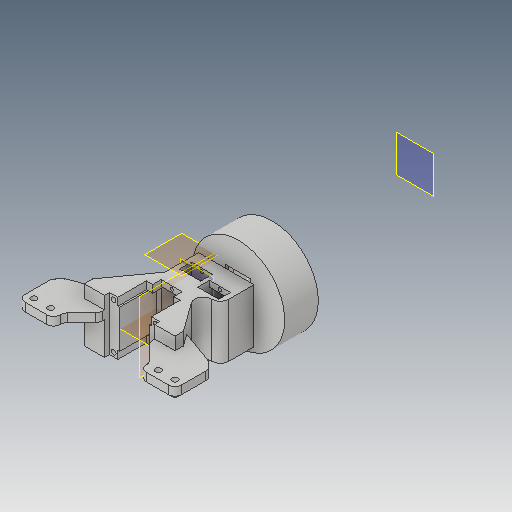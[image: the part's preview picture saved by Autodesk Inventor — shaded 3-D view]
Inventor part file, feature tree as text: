
AUTODESK INVENTOR PART (.ipt)
format: ipt  version: 2018 (Build 220112000, 112)  size: 501,248 bytes
history: native  units: mm
features: extrude x22, sketch x19, plane x6, mirror x5, fillet x2
ambient origin geometry x8: Origin, YZ Plane, XZ Plane, XY Plane, X Axis, Y Axis, Z Axis, Center Point
bodies: Solid1 (feature_tree)
feature tree (54):
  extrude  "base"  Depth=32.0mm
  extrude  "servo_place"  Depth=25.0mm
  extrude  "screws_servo"  Depth=6.25mm
  plane  "Work Plane1"
  extrude  "pilars_top"  Depth=12.5mm
  extrude  "base_top"  Depth=18.0mm
  extrude  "screw_hole"  Depth=2.0mm
  plane  "Work Plane2"
  plane  "Work Plane6"
  plane  "Work Plane5"
  extrude  "Extrusion16"  Depth=17.0mm TaperAngle=0.0deg
  plane  "Work Plane3"
  plane  "Work Plane4"
  mirror  "Mirror1"
  mirror  "Mirror2"
  extrude  "Extrusion18"  Depth=18.0mm
  extrude  "Extrusion19"  Depth=5.0mm TaperAngle=0.0deg
  extrude  "Extrusion20"  Depth=5.0mm TaperAngle=0.0deg
  mirror  "Mirror3"
  mirror  "Mirror4"
  extrude  "Extrusion21"  Depth=5.0mm
  extrude  "Extrusion22"  [1 undecoded]
  extrude  "Extrusion23"  Depth=4.6mm TaperAngle=0.0deg
  extrude  "Extrusion11"  Depth=12.5mm
  extrude  "Extrusion24"  Depth=10.0mm
  fillet  "Fillet5"  Radius=20.0mm
  mirror  "Mirror5"
  extrude  "Extrusion25"  Depth=5.0mm
  extrude  "Extrusion26"  Depth=3.0mm TaperAngle=0.0deg
  extrude  "Extrusion27"  Depth=2.5mm
  fillet  "Fillet6"  Radius=2.8mm
  extrude  "Extrusion28"  Depth=2.0mm
  extrude  "Extrusion29"  Depth=12.5mm
  sketch  "Sketch30"  dims[d117=5.0mm d118=0.0mm d119=11.75mm d120=12.5mm d121=23.5mm d122=12.5mm d123=10.0mm d124=0.0mm d125=7.0mm d126=10.0mm d127=0.0mm d131=27.0mm d132=27.0mm d133=10.0mm d134=0.0mm d135=10.0mm d136=15.0mm d137=3.5mm d138=10.0mm d139=3.5mm d140=3.0mm d141=15.0mm d142=135.0deg d143=6.0mm d144=21.0mm d145=20.0mm d146=6.0mm d147=5.0mm d148=0.0mm d149=4.0mm d150=12.5mm d151=25.0mm d152=5.0mm d153=0.0mm d154=15.0mm d155=0.0mm d156=3.0mm d157=12.5mm d158=12.5mm d159=90.0deg d160=25.0mm d161=90.0deg d162=12.5mm d163=18.0mm d164=0.0mm d165=5.0mm d166=1.8mm d167=90.0deg d168=2.0mm d169=1.8mm d170=90.0deg d171=2.0mm d172=18.0mm d173=0.0mm d174=7.0mm d175=18.0mm d176=0.0mm d177=7.5mm d178=90.0deg d179=50.0mm d180=55.0mm d181=20.0mm d182=0.0mm d183=5.0mm d184=2.0mm d185=90.0deg d186=15.0mm d187=90.0deg d188=2.0mm d189=0.0mm]
  extrude  "Extrusion30"  Depth=23.5mm
  extrude  "Extrusion31"  Depth=12.5mm
  sketch  "Sketch1"  dims[d0=18.0mm d1=32.0mm]
  sketch  "Sketch2"  dims[d2=25.0mm d3=0.0mm d4=11.5mm]
  sketch  "Sketch3"  dims[d5=90.0deg d6=6.25mm]
  sketch  "Sketch6"  dims[d7=23.0mm d8=12.5mm]
  sketch  "Sketch9"  dims[d9=18.0mm d10=0.0mm d11=2.8mm]
  sketch  "Sketch16"  dims[d12=2.0mm d13=2.8mm]
  sketch  "Sketch18"  dims[d14=2.0mm d15=17.0mm d16=0.0mm]
  sketch  "Sketch19"  dims[d26=20.0mm d27=0.0mm d39=18.0mm]
  sketch  "Sketch20"  dims[d40=18.0mm d41=5.0mm d42=0.0mm]
  sketch  "Sketch21"  dims[d47=5.0mm d48=0.0mm d55=5.0mm d56=0.0mm]
  sketch  "Sketch22"  dims[d60=2.5mm d61=5.0mm]
  sketch  "Sketch23"  dims[d62=5.0mm d63=-10.0mm]
  sketch  "Sketch24"  dims[d95=25.0mm d96=4.6mm d97=0.0mm]
  sketch  "Sketch25"  dims[d98=-16.0mm d100=12.5mm]
  sketch  "Sketch26"  dims[d105=5.0mm d106=10.0mm d107=20.0mm]
  sketch  "Sketch27"  dims[d108=10.0mm d109=0.0mm d110=5.0mm]
  sketch  "Sketch28"  dims[d111=30.0mm d112=3.0mm d113=0.0mm]
  sketch  "Sketch29"  dims[d114=2.5mm d115=2.5mm d116=2.8mm]
note: 1 required parameter value undecoded (feature->parameter linkage not recoverable at this tier; creation-order binding heuristic only, values carry confidence <= 0.55)
